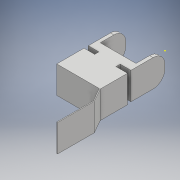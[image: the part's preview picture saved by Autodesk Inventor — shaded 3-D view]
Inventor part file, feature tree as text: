
AUTODESK INVENTOR PART (.ipt)
format: ipt  version: 2017 (Build 210142000, 142)  size: 167,424 bytes
history: native  units: mm
features: sketch x8, extrude x7, chamfer x2, other x1, fillet x1
ambient origin geometry x8: Origin, YZ Plane, XZ Plane, XY Plane, X Axis, Y Axis, Z Axis, Center Point
bodies: Body1 (feature_tree)
feature tree (19):
  other  "ソリッド1"
  extrude  "押し出し1"  Depth=0.04mm
  extrude  "押し出し2"  Depth=0.32mm
  extrude  "押し出し3"  Depth=0.04mm
  extrude  "押し出し4"  Depth=0.3mm TaperAngle=0.0deg
  extrude  "押し出し5"  Depth=0.1mm TaperAngle=0.0deg
  extrude  "押し出し6"  Depth=0.25mm
  chamfer  "面取り1"  Distance=0.05mm
  chamfer  "面取り2"  Distance=0.32mm
  extrude  "押し出し7"  Depth=0.01mm TaperAngle=0.0deg
  fillet  "フィレット1"  Radius=0.1mm
  sketch  "スケッチ8"
  sketch  "スケッチ1"
  sketch  "スケッチ2"
  sketch  "スケッチ3"
  sketch  "スケッチ4"
  sketch  "スケッチ5"
  sketch  "スケッチ6"
  sketch  "スケッチ7"
